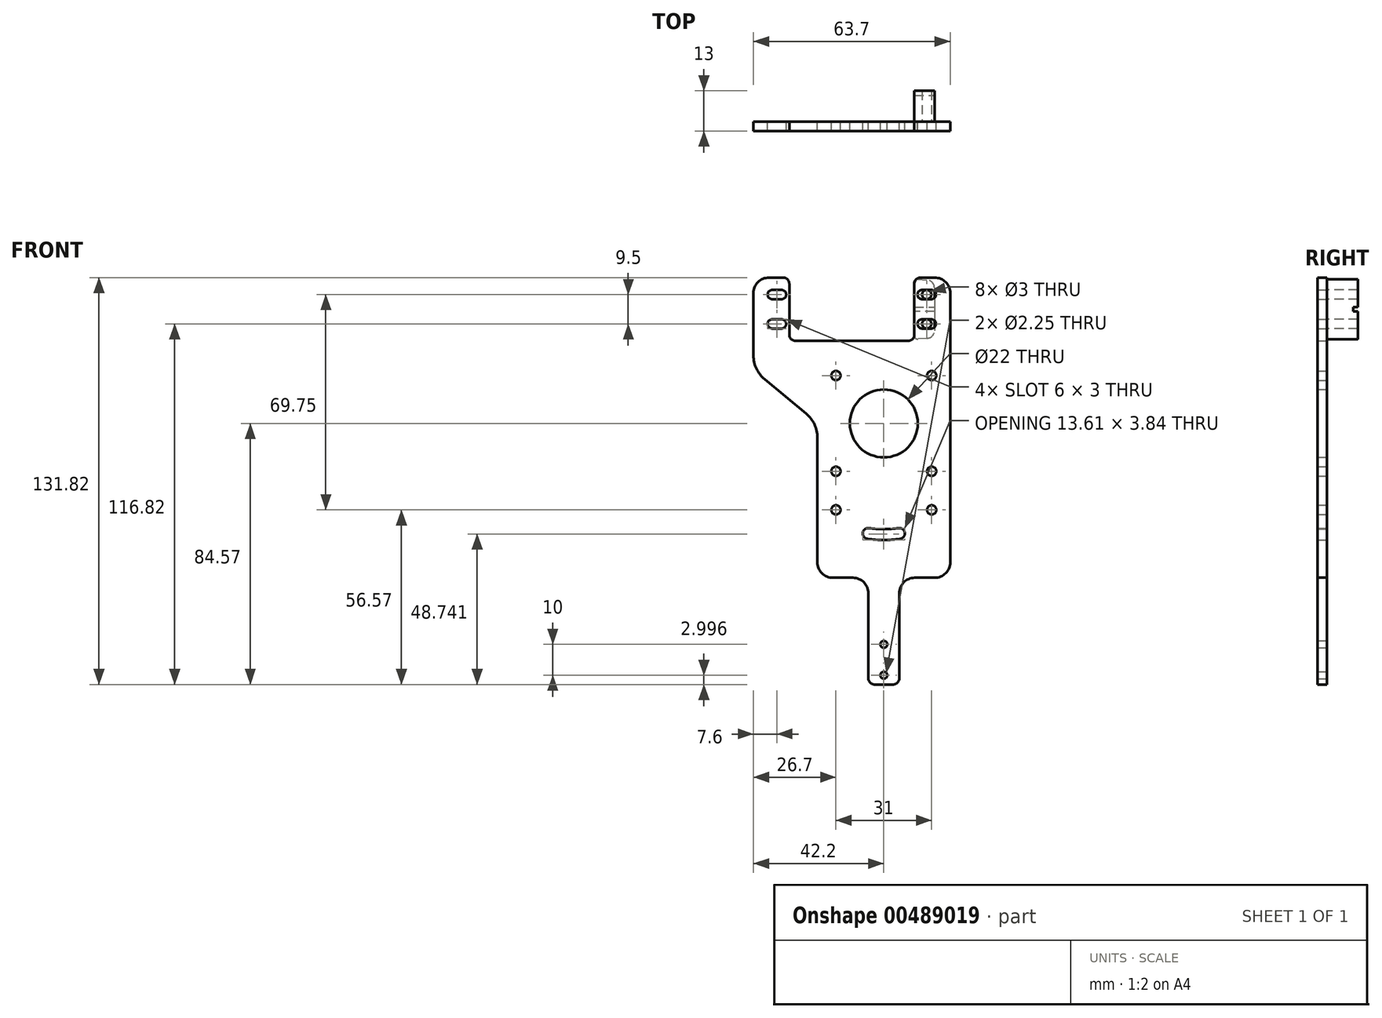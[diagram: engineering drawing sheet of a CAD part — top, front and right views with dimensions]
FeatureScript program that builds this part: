
annotation { "Feature Type Name" : "Feature", "Feature Type Description" : "" }
export const myFeature = defineFeature(function(context is Context, id is Id, definition is map)
    precondition{}
    {
        {
            var Q0;
            Q0=qCreatedBy(makeId("Front.planeOp"),FACE);
            var sketch = newSketch(context, id + "F0", { "sketchPlane" : qUnion([Q0])});
            skLineSegment(sketch, "E0", {"start": v(0, 45.16) * mm, "end": v(0, -78.26) * mm, "construction": true});
            skLineSegment(sketch, "E1", {"start": v(-43, 0) * mm, "end": v(26.64, 0) * mm, "construction": true});
            skCircle(sketch, "E2", {"center": v(0, 0) * mm, "radius": 3.5 * mm, "construction": true});
            skLineSegment(sketch, "E3", {"start": v(-3.05, 24.93) * mm, "end": v(28.89, -79.52) * mm, "construction": true});
            skLineSegment(sketch, "E4", {"start": v(1.45, 7.22) * mm, "end": v(8.27, -15.1) * mm, "construction": true});
            skLineSegment(sketch, "E5", {"start": v(3.28, 7.22) * mm, "end": v(10.1, -15.1) * mm, "construction": true});
            skSolve(sketch);
        }
        {
            var Q0;
            Q0=qCreatedBy(makeId("Front.planeOp"),FACE);
            var sketch = newSketch(context, id + "F1", { "sketchPlane" : qUnion([Q0])});
            skCircle(sketch, "E6", {"center": v(15.5, 15.5) * mm, "radius": 1.5 * mm});
            skLineSegment(sketch, "E7", {"start": v(21.5, -45) * mm, "end": v(21.5, 42.25) * mm});
            skPoint(sketch, "E8", {"position": v(0, -50) * mm});
            skArc(sketch, "E9", {"start": v(4.83, -33.9) * mm, "mid": v(2.42, -34.16) * mm, "end": v(0, -34.25) * mm});
            skArc(sketch, "E10", {"start": v(5.32, -37.37) * mm, "mid": v(2.67, -37.66) * mm, "end": v(0, -37.75) * mm});
            skArc(sketch, "E11", {"start": v(4.83, -33.9) * mm, "mid": v(6.8, -35.4) * mm, "end": v(5.32, -37.37) * mm});
            skArc(sketch, "E12", {"start": v(8.38, -35) * mm, "mid": v(-0.1, -36) * mm, "end": v(-8.59, -34.96) * mm, "construction": true});
            skCircle(sketch, "E13.MirrorC", {"center": v(15.5, -15.5) * mm, "radius": 1.5 * mm});
            skCircle(sketch, "E14.MirrorC", {"center": v(-15.5, 15.5) * mm, "radius": 1.5 * mm});
            skCircle(sketch, "E15.MirrorC", {"center": v(-15.5, -15.5) * mm, "radius": 1.5 * mm});
            skLineSegment(sketch, "E16.MirrorCS", {"start": v(-21.5, -45) * mm, "end": v(-21.5, -4.56) * mm});
            skArc(sketch, "E17.MirrorCS", {"start": v(-5.32, -37.37) * mm, "mid": v(-2.67, -37.66) * mm, "end": v(0, -37.75) * mm});
            skArc(sketch, "E18.MirrorCS", {"start": v(-4.83, -33.9) * mm, "mid": v(-6.8, -35.4) * mm, "end": v(-5.32, -37.37) * mm});
            skArc(sketch, "E19.MirrorCS", {"start": v(-4.83, -33.9) * mm, "mid": v(-2.42, -34.16) * mm, "end": v(0, -34.25) * mm});
            skLineSegment(sketch, "E20", {"start": v(16.5, 47.25) * mm, "end": v(11.9, 47.25) * mm});
            skLineSegment(sketch, "E21", {"start": v(-42.2, 42.25) * mm, "end": v(-42.2, 22.02) * mm});
            skLineSegment(sketch, "E22", {"start": v(-10.35, 28.4) * mm, "end": v(-10.35, 46.94) * mm, "construction": true});
            skLineSegment(sketch, "E23", {"start": v(22.97, 37) * mm, "end": v(-42.76, 37) * mm, "construction": true});
            skCircle(sketch, "E24", {"center": v(0, 0) * mm, "radius": 11 * mm});
            skLineSegment(sketch, "E25", {"start": v(-16.5, -50) * mm, "end": v(-10, -50) * mm});
            skPoint(sketch, "E26.visualSharp", {"position": v(21.06, 47.25) * mm});
            skArc(sketch, "E26.filletArc", {"start": v(21.5, 42.25) * mm, "mid": v(20.04, 45.79) * mm, "end": v(16.5, 47.25) * mm});
            skPoint(sketch, "E27.visualSharp", {"position": v(-42.2, 47.25) * mm});
            skArc(sketch, "E27.filletArc", {"start": v(-37.2, 47.25) * mm, "mid": v(-40.74, 45.79) * mm, "end": v(-42.2, 42.25) * mm});
            skArc(sketch, "E28", {"start": v(-36.1, 33.75) * mm, "mid": v(-37.6, 32.25) * mm, "end": v(-36.1, 30.75) * mm});
            skLineSegment(sketch, "E29", {"start": v(-38.59, 14.32) * mm, "end": v(-25.11, 3.14) * mm});
            skPoint(sketch, "E30.visualSharp", {"position": v(-21.5, 0.14) * mm});
            skArc(sketch, "E30.filletArc", {"start": v(-21.5, -4.56) * mm, "mid": v(-22.45, -0.3) * mm, "end": v(-25.11, 3.14) * mm});
            skPoint(sketch, "E31.visualSharp", {"position": v(-42.2, 17.32) * mm});
            skArc(sketch, "E31.filletArc", {"start": v(-42.2, 22.02) * mm, "mid": v(-41.25, 17.76) * mm, "end": v(-38.59, 14.32) * mm});
            skArc(sketch, "E32", {"start": v(-33.1, 30.75) * mm, "mid": v(-31.6, 32.25) * mm, "end": v(-33.1, 33.75) * mm});
            skLineSegment(sketch, "E33", {"start": v(-33.1, 33.75) * mm, "end": v(-36.1, 33.75) * mm});
            skLineSegment(sketch, "E34", {"start": v(-33.1, 30.75) * mm, "end": v(-36.1, 30.75) * mm});
            skArc(sketch, "E35.MirrorCS", {"start": v(-36.1, 40.25) * mm, "mid": v(-37.6, 41.75) * mm, "end": v(-36.1, 43.25) * mm});
            skLineSegment(sketch, "E36.MirrorCS", {"start": v(-33.1, 40.25) * mm, "end": v(-36.1, 40.25) * mm});
            skArc(sketch, "E37.MirrorCS", {"start": v(-33.1, 43.25) * mm, "mid": v(-31.6, 41.75) * mm, "end": v(-33.1, 40.25) * mm});
            skLineSegment(sketch, "E38.MirrorCS", {"start": v(-33.1, 43.25) * mm, "end": v(-36.1, 43.25) * mm});
            skArc(sketch, "E39.MirrorCS", {"start": v(12.4, 30.75) * mm, "mid": v(10.9, 32.25) * mm, "end": v(12.4, 33.75) * mm});
            skLineSegment(sketch, "E40.MirrorCS", {"start": v(12.4, 30.75) * mm, "end": v(15.4, 30.75) * mm});
            skLineSegment(sketch, "E41.MirrorCS", {"start": v(12.4, 33.75) * mm, "end": v(15.4, 33.75) * mm});
            skArc(sketch, "E42.MirrorCS", {"start": v(15.4, 33.75) * mm, "mid": v(16.9, 32.25) * mm, "end": v(15.4, 30.75) * mm});
            skLineSegment(sketch, "E43.MirrorCS", {"start": v(12.4, 40.25) * mm, "end": v(15.4, 40.25) * mm});
            skArc(sketch, "E44.MirrorCS", {"start": v(15.4, 40.25) * mm, "mid": v(16.9, 41.75) * mm, "end": v(15.4, 43.25) * mm});
            skArc(sketch, "E45.MirrorCS", {"start": v(12.4, 43.25) * mm, "mid": v(10.9, 41.75) * mm, "end": v(12.4, 40.25) * mm});
            skLineSegment(sketch, "E46.MirrorCS", {"start": v(12.4, 43.25) * mm, "end": v(15.4, 43.25) * mm});
            skCircle(sketch, "E47", {"center": v(5.32, -35.6) * mm, "radius": 1.5 * mm, "construction": true});
            skLineSegment(sketch, "E48", {"start": v(0, 0) * mm, "end": v(6.18, -41.34) * mm, "construction": true});
            skCircle(sketch, "E49", {"center": v(-34.6, 32.25) * mm, "radius": 1.5 * mm, "construction": true});
            skCircle(sketch, "E50.MirrorC", {"center": v(-34.6, 41.75) * mm, "radius": 1.5 * mm, "construction": true});
            skCircle(sketch, "E51.MirrorC", {"center": v(13.9, 32.25) * mm, "radius": 1.5 * mm, "construction": true});
            skCircle(sketch, "E52.MirrorC", {"center": v(13.9, 41.75) * mm, "radius": 1.5 * mm, "construction": true});
            skCircle(sketch, "E53", {"center": v(15.5, -28) * mm, "radius": 1.5 * mm});
            skCircle(sketch, "E54.MirrorC", {"center": v(-15.5, -28) * mm, "radius": 1.5 * mm});
            skLineSegment(sketch, "E55", {"start": v(-28.6, 26.75) * mm, "end": v(7.9, 26.75) * mm});
            skLineSegment(sketch, "E56", {"start": v(-30.6, 45.25) * mm, "end": v(-30.6, 28.75) * mm});
            skLineSegment(sketch, "E57", {"start": v(9.9, 45.25) * mm, "end": v(9.9, 28.75) * mm});
            skLineSegment(sketch, "E58.trimOffspring", {"start": v(-32.6, 47.25) * mm, "end": v(-37.2, 47.25) * mm});
            skPoint(sketch, "E59.visualSharp", {"position": v(-30.6, 47.25) * mm});
            skArc(sketch, "E59.filletArc", {"start": v(-30.6, 45.25) * mm, "mid": v(-31.19, 46.66) * mm, "end": v(-32.6, 47.25) * mm});
            skPoint(sketch, "E60.visualSharp", {"position": v(9.9, 47.25) * mm});
            skArc(sketch, "E60.filletArc", {"start": v(11.9, 47.25) * mm, "mid": v(10.49, 46.66) * mm, "end": v(9.9, 45.25) * mm});
            skPoint(sketch, "E61.visualSharp", {"position": v(-30.6, 26.75) * mm});
            skArc(sketch, "E61.filletArc", {"start": v(-30.6, 28.75) * mm, "mid": v(-30.01, 27.34) * mm, "end": v(-28.6, 26.75) * mm});
            skPoint(sketch, "E62.visualSharp", {"position": v(9.9, 26.75) * mm});
            skArc(sketch, "E62.filletArc", {"start": v(7.9, 26.75) * mm, "mid": v(9.31, 27.34) * mm, "end": v(9.9, 28.75) * mm});
            skLineSegment(sketch, "E63", {"start": v(-36.07, -22) * mm, "end": v(-55, -22) * mm, "construction": true});
            skLineSegment(sketch, "E64", {"start": v(-15, -66.45) * mm, "end": v(-53.61, -66.45) * mm, "construction": true});
            skCircle(sketch, "E65", {"center": v(0, -71.57) * mm, "radius": 1.13 * mm});
            skCircle(sketch, "E66", {"center": v(0, -81.57) * mm, "radius": 1.13 * mm});
            skLineSegment(sketch, "E67", {"start": v(-5, -55) * mm, "end": v(-5, -82.57) * mm});
            skLineSegment(sketch, "E68", {"start": v(-3, -84.57) * mm, "end": v(3, -84.57) * mm});
            skLineSegment(sketch, "E69", {"start": v(5, -82.57) * mm, "end": v(5, -55) * mm});
            skLineSegment(sketch, "E70", {"start": v(10, -50) * mm, "end": v(16.5, -50) * mm});
            skPoint(sketch, "E71.visualSharp", {"position": v(-5, -84.57) * mm});
            skArc(sketch, "E71.filletArc", {"start": v(-5, -82.57) * mm, "mid": v(-4.41, -83.99) * mm, "end": v(-3, -84.57) * mm});
            skPoint(sketch, "E72.visualSharp", {"position": v(5, -84.57) * mm});
            skArc(sketch, "E72.filletArc", {"start": v(3, -84.57) * mm, "mid": v(4.41, -83.99) * mm, "end": v(5, -82.57) * mm});
            skPoint(sketch, "E73.visualSharp", {"position": v(-21.5, -50) * mm});
            skArc(sketch, "E73.filletArc", {"start": v(-21.5, -45) * mm, "mid": v(-20.04, -48.54) * mm, "end": v(-16.5, -50) * mm});
            skPoint(sketch, "E74.visualSharp", {"position": v(-5, -50) * mm});
            skArc(sketch, "E74.filletArc", {"start": v(-5, -55) * mm, "mid": v(-6.46, -51.46) * mm, "end": v(-10, -50) * mm});
            skPoint(sketch, "E75.visualSharp", {"position": v(5, -50) * mm});
            skArc(sketch, "E75.filletArc", {"start": v(10, -50) * mm, "mid": v(6.46, -51.46) * mm, "end": v(5, -55) * mm});
            skPoint(sketch, "E76.visualSharp", {"position": v(21.5, -50) * mm});
            skArc(sketch, "E76.filletArc", {"start": v(16.5, -50) * mm, "mid": v(20.04, -48.54) * mm, "end": v(21.5, -45) * mm});
            skSolve(sketch);
        }
        {
            var Q0;
            Q0=qSketchRegion(id+"F1",true);
            extrude(context, id + "F2", {"entities" : qUnion([Q0]), "depth" : 3 * mm});
        }
        {
            var Q0;
            Q0=qCreatedBy(makeId("Front.planeOp"),FACE);
            var sketch = newSketch(context, id + "F3", { "sketchPlane" : qUnion([Q0])});
            skLineSegment(sketch, "E77", {"start": v(16.4, 46.25) * mm, "end": v(16.4, 27.75) * mm});
            skLineSegment(sketch, "E78", {"start": v(16.4, 27.75) * mm, "end": v(9.9, 27.25) * mm});
            skLineSegment(sketch, "E79", {"start": v(9.9, 27.25) * mm, "end": v(9.9, 46.75) * mm});
            skLineSegment(sketch, "E80", {"start": v(9.9, 46.75) * mm, "end": v(16.4, 46.25) * mm});
            skCircle(sketch, "E81", {"center": v(13.9, 32.25) * mm, "radius": 1.5 * mm});
            skCircle(sketch, "E82.MirrorC", {"center": v(13.9, 41.75) * mm, "radius": 1.5 * mm});
            skLineSegment(sketch, "E83", {"start": v(13.9, 47.55) * mm, "end": v(13.9, 25.9) * mm, "construction": true});
            skSolve(sketch);
        }
        {
            var Q0;
            Q0=qSketchRegion(id+"F3",true);
            extrude(context, id + "F4", {"entities" : qUnion([Q0]), "oppositeDirection" : true, "depth" : 10 * mm});
        }
        {
            var Q0;
            Q0=makeQuery(id+"F4.opExtrude","CAP_FACE",FACE,{"disambiguationData":[OSD([sQuery(id+"F3.wireOp",EDGE,"E77"),sQuery(id+"F3.wireOp",EDGE,"E78"),sQuery(id+"F3.wireOp",EDGE,"E79"),sQuery(id+"F3.wireOp",EDGE,"E80"),sQuery(id+"F3.wireOp",EDGE,"E81"),sQuery(id+"F3.wireOp",EDGE,"E82.MirrorC")])],"isStart":false});
            var sketch = newSketch(context, id + "F5", { "sketchPlane" : qUnion([Q0])});
            skLineSegment(sketch, "E84", {"start": v(40.1, -4.41) * mm, "end": v(22.9, -4.41) * mm, "construction": true});
            skLineSegment(sketch, "E85", {"start": v(-9.9, 36.25) * mm, "end": v(-9.9, 37.75) * mm});
            skLineSegment(sketch, "E86", {"start": v(-9.9, 37.75) * mm, "end": v(-16.4, 37.75) * mm});
            skLineSegment(sketch, "E87", {"start": v(-16.4, 37.75) * mm, "end": v(-16.4, 36.25) * mm});
            skLineSegment(sketch, "E88", {"start": v(-16.4, 36.25) * mm, "end": v(-9.9, 36.25) * mm});
            skSolve(sketch);
        }
        {
            var Q0;
            Q0=qSketchRegion(id+"F5",true);
            extrude(context, id + "F6", {"entities" : qUnion([Q0]), "operationType" : NewBodyOperationType.REMOVE, "oppositeDirection" : true, "depth" : 1.5 * mm});
        }
        {
            var Q0;
            Q0=makeQuery(id+"F4.opExtrude","SWEPT_EDGE",EDGE,{"disambiguationData":[OSD([sQuery(id+"F3.wireOp",EDGE,"E79"),sQuery(id+"F3.wireOp",EDGE,"E80")])]});
            var Q1;
            Q1=makeQuery(id+"F4.opExtrude","SWEPT_EDGE",EDGE,{"disambiguationData":[OSD([sQuery(id+"F3.wireOp",EDGE,"E78"),sQuery(id+"F3.wireOp",EDGE,"E79")])]});
            fillet(context, id + "F7", {"entities" : qUnion([Q0, Q1]), "radius" : 1 * mm, "tangentPropagation" : true, "allowEdgeOverflow" : false});
        }
        {
            var Q0;
            Q0=makeQuery(id+"F4.opExtrude","SWEPT_EDGE",EDGE,{"disambiguationData":[OSD([sQuery(id+"F3.wireOp",EDGE,"E77"),sQuery(id+"F3.wireOp",EDGE,"E78")])]});
            var Q1;
            Q1=makeQuery(id+"F4.opExtrude","SWEPT_EDGE",EDGE,{"disambiguationData":[OSD([sQuery(id+"F3.wireOp",EDGE,"E77"),sQuery(id+"F3.wireOp",EDGE,"E80")])]});
            fillet(context, id + "F8", {"entities" : qUnion([Q0, Q1]), "radius" : 2.5 * mm, "tangentPropagation" : true, "allowEdgeOverflow" : false});
        }
    });
